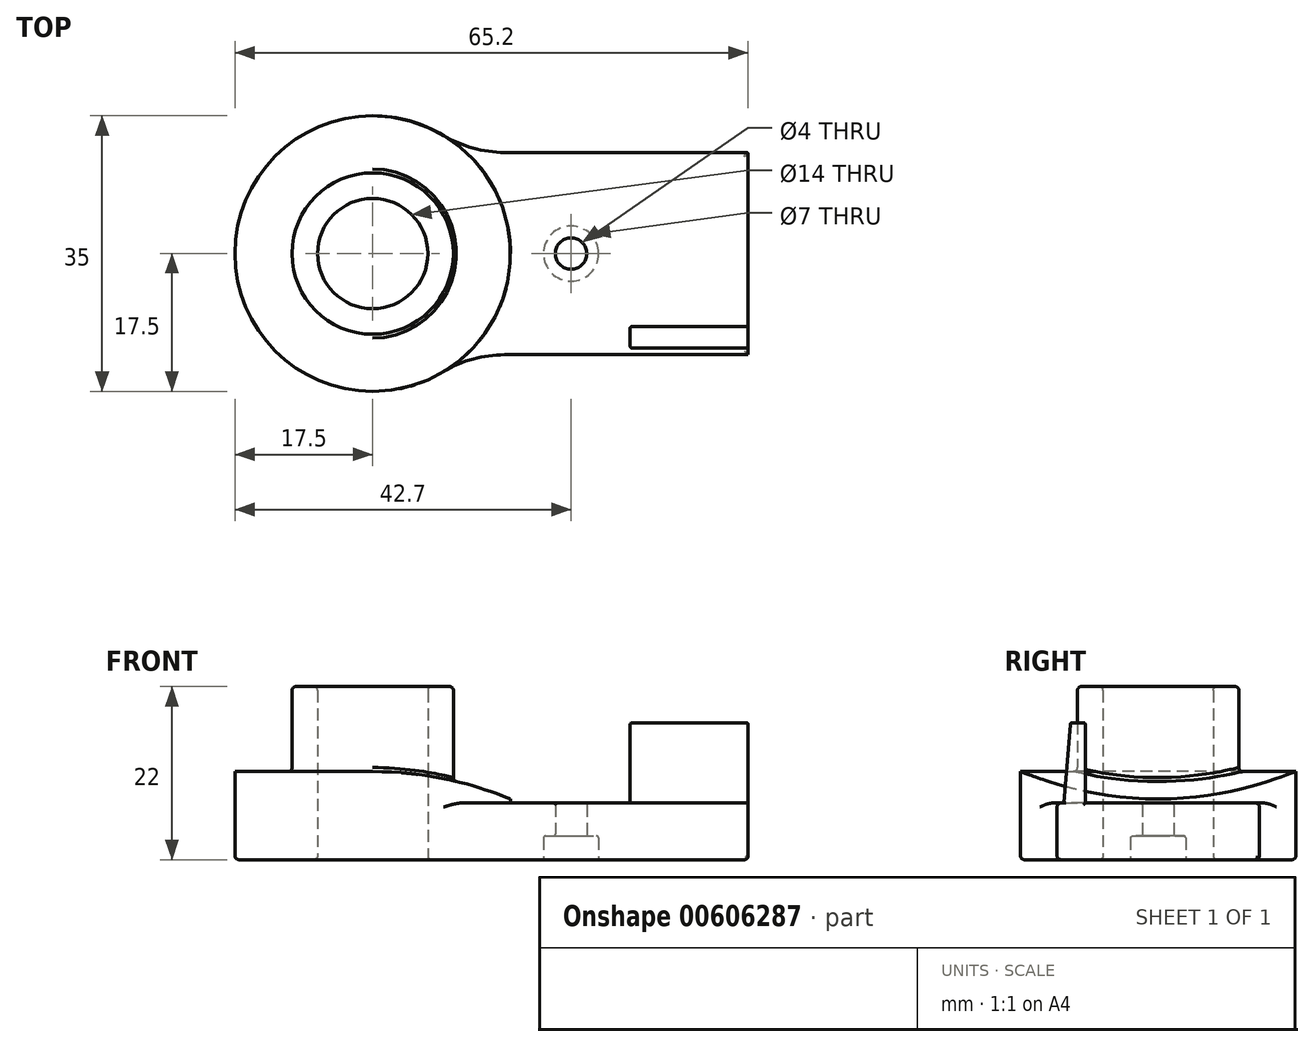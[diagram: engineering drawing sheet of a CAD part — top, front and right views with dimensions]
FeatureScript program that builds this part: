
annotation { "Feature Type Name" : "Feature", "Feature Type Description" : "" }
export const myFeature = defineFeature(function(context is Context, id is Id, definition is map)
    precondition{}
    {
        {
            var Q0;
            Q0=qCreatedBy(makeId("Top.planeOp"),FACE);
            var sketch = newSketch(context, id + "F0", { "sketchPlane" : qUnion([Q0])});
            skArc(sketch, "E0", {"start": v(11.88, 12.85) * mm, "mid": v(-17.5, 0) * mm, "end": v(11.88, -12.85) * mm});
            skLineSegment(sketch, "E1.bottom", {"start": v(11.88, 12.85) * mm, "end": v(47.7, 12.85) * mm});
            skLineSegment(sketch, "E1.top", {"start": v(11.88, -12.85) * mm, "end": v(47.7, -12.85) * mm});
            skLineSegment(sketch, "E1.right", {"start": v(47.7, 12.85) * mm, "end": v(47.7, -12.85) * mm});
            skLineSegment(sketch, "E2", {"start": v(47.7, 0) * mm, "end": v(0, 0) * mm, "construction": true});
            skCircle(sketch, "E3", {"center": v(25.2, 0) * mm, "radius": 2 * mm});
            skCircle(sketch, "E4", {"center": v(0, 0) * mm, "radius": 7 * mm});
            skPoint(sketch, "E5.orphan", {"position": v(0, 12.85) * mm});
            skPoint(sketch, "E6.trimOffspring.end.orphan", {"position": v(0, -12.85) * mm});
            skSolve(sketch);
        }
        {
            var Q0;
            Q0 = qSketchRegion(id + "F0", true);
            extrude(context, id + "F1", {"entities" : qUnion([Q0]), "depth" : 7.2 * mm, "offsetDistance" : 25 * mm});
        }
        {
            var Q0;
            Q0=makeQuery(id+"F1.opExtrude","SWEPT_FACE",FACE,{"disambiguationData":[OSD([sQuery(id+"F0.wireOp",EDGE,"E1.right")])]});
            var sketch = newSketch(context, id + "F2", { "sketchPlane" : qUnion([Q0])});
            skLineSegment(sketch, "E7", {"start": v(-9.25, 7.2) * mm, "end": v(-9.25, 17.4) * mm});
            skLineSegment(sketch, "E8", {"start": v(-9.25, 17.4) * mm, "end": v(-11.15, 17.4) * mm});
            skLineSegment(sketch, "E9", {"start": v(-11.15, 17.4) * mm, "end": v(-12, 7.2) * mm});
            skLineSegment(sketch, "E10", {"start": v(-12, 7.2) * mm, "end": v(-9.25, 7.2) * mm});
            skSolve(sketch);
        }
        {
            var Q0;
            Q0=makeQuery(id+"F2.imprint","IMPRINT",FACE,{"disambiguationData":[TD([[makeQuery(id+"F2.imprint","IMPRINT",EDGE,{"derivedFrom":sQuery(id+"F2.wireOp",EDGE,"E7")}),1.0]])]});
            extrude(context, id + "F3", {"entities" : qUnion([Q0]), "operationType" : NewBodyOperationType.ADD, "oppositeDirection" : true, "depth" : 15 * mm, "offsetDistance" : 25 * mm});
        }
        {
            var Q0;
            Q0=makeQuery(id+"F1.opExtrude","CAP_FACE",FACE,{"disambiguationData":[OSD([sQuery(id+"F0.wireOp",EDGE,"E0"),sQuery(id+"F0.wireOp",EDGE,"E1.bottom"),sQuery(id+"F0.wireOp",EDGE,"E1.top"),sQuery(id+"F0.wireOp",EDGE,"E1.right"),sQuery(id+"F0.wireOp",EDGE,"E3"),sQuery(id+"F0.wireOp",EDGE,"E4")])],"isStart":false});
            var sketch = newSketch(context, id + "F4", { "sketchPlane" : qUnion([Q0])});
            skCircle(sketch, "E11.0", {"center": v(0, 0) * mm, "radius": 7 * mm});
            skCircle(sketch, "E12", {"center": v(0, 0) * mm, "radius": 17.5 * mm});
            skSolve(sketch);
        }
        {
            var Q0;
            Q0 = qSketchRegion(id + "F4", true);
            extrude(context, id + "F5", {"entities" : qUnion([Q0]), "operationType" : NewBodyOperationType.ADD, "depth" : 4 * mm, "offsetDistance" : 25 * mm});
        }
        {
            var Q0;
            Q0=qCreatedBy(makeId("Front.planeOp"),FACE);
            var sketch = newSketch(context, id + "F6", { "sketchPlane" : qUnion([Q0])});
            skArc(sketch, "E13", {"start": v(17.5, 7.7) * mm, "mid": v(8.92, 10.32) * mm, "end": v(0, 11.2) * mm});
            skLineSegment(sketch, "E14", {"start": v(0, 11.2) * mm, "end": v(0, 14.73) * mm});
            skLineSegment(sketch, "E15", {"start": v(0, 14.73) * mm, "end": v(20.16, 14.73) * mm});
            skLineSegment(sketch, "E16", {"start": v(20.16, 14.73) * mm, "end": v(17.5, 7.7) * mm});
            skSolve(sketch);
        }
        {
            var Q0;
            Q0=makeQuery(id+"F6.imprint","IMPRINT",FACE,{"disambiguationData":[TD([[makeQuery(id+"F6.imprint","IMPRINT",EDGE,{"derivedFrom":sQuery(id+"F6.wireOp",EDGE,"E13")}),-1.0]])]});
            extrude(context, id + "F7", {"entities" : qUnion([Q0]), "operationType" : NewBodyOperationType.REMOVE, "endBound" : BoundingType.SYMMETRIC, "oppositeDirection" : true, "depth" : 35 * mm, "offsetDistance" : 25 * mm});
        }
        {
            var Q0;
            Q0=qCreatedBy(makeId("Top.planeOp"),FACE);
            var sketch = newSketch(context, id + "F8", { "sketchPlane" : qUnion([Q0])});
            skCircle(sketch, "E17", {"center": v(0, 0) * mm, "radius": 10.25 * mm});
            skCircle(sketch, "E18", {"center": v(0, 0) * mm, "radius": 7 * mm});
            skSolve(sketch);
        }
        {
            var Q0;
            Q0 = qSketchRegion(id + "F8", true);
            extrude(context, id + "F9", {"entities" : qUnion([Q0]), "operationType" : NewBodyOperationType.ADD, "depth" : 22 * mm, "offsetDistance" : 25 * mm});
        }
        {
            var Q0;
            Q0=makeQuery(id+"F1.opExtrude","SWEPT_EDGE",EDGE,{"disambiguationData":[OSD([sQuery(id+"F0.wireOp",EDGE,"E0"),sQuery(id+"F0.wireOp",EDGE,"E1.top")])]});
            var Q1;
            Q1=makeQuery(id+"F1.opExtrude","SWEPT_EDGE",EDGE,{"disambiguationData":[OSD([sQuery(id+"F0.wireOp",EDGE,"E0"),sQuery(id+"F0.wireOp",EDGE,"E1.bottom")])]});
            fillet(context, id + "F10", {"entities" : qUnion([Q0, Q1]), "radius" : 15 * mm, "tangentPropagation" : true, "allowEdgeOverflow" : false});
        }
        {
            var Q0;
            Q0=makeQuery(id+"FCpYSeTeSg7XSQh_1.1.F7.boolean.opBoolean","INTERSECT",EDGE,{"derivedFrom":[makeQuery(id+"F5.boolean.opBoolean","MERGE",FACE,{"derivedFrom":[makeQuery(id+"F1.opExtrude","SWEPT_FACE",FACE,{"disambiguationData":[OSD([sQuery(id+"F0.wireOp",EDGE,"E0")])]}),makeQuery(id+"F5.opExtrude","SWEPT_FACE",FACE,{"disambiguationData":[OSD([sQuery(id+"F4.wireOp",EDGE,"E12")])]})]}),makeQuery(id+"FCpYSeTeSg7XSQh_1.1.F7.opExtrude","SWEPT_FACE",FACE,{"disambiguationData":[OSD([sQuery(id+"F6.wireOp",EDGE,"E13")])]})]});
            var Q1;
            {var subQ0=sQuery(id+"F6.wireOp",EDGE,"E13");Q1=makeQuery(id+"F9.boolean.opBoolean","INTERSECT",EDGE,{"derivedFrom":[makeQuery(id+"FCpYSeTeSg7XSQh_1.1.F7.boolean.opBoolean","MERGE",FACE,{"derivedFrom":[makeQuery(id+"F7.boolean.opBoolean","COPY",FACE,{"derivedFrom":makeQuery(id+"F7.opExtrude","SWEPT_FACE",FACE,{"disambiguationData":[OSD([subQ0])]})}),makeQuery(id+"FCpYSeTeSg7XSQh_1.1.F7.opExtrude","SWEPT_FACE",FACE,{"disambiguationData":[OSD([subQ0])]})]}),makeQuery(id+"F9.opExtrude","SWEPT_FACE",FACE,{"disambiguationData":[OSD([sQuery(id+"F8.wireOp",EDGE,"E17")])]})]});}
            var Q2;
            Q2=makeQuery(id+"F9.opExtrude","CAP_EDGE",EDGE,{"disambiguationData":[OSD([sQuery(id+"F8.wireOp",EDGE,"E17")])],"isStart":false});
            var Q3;
            Q3=makeQuery(id+"F9.opExtrude","CAP_EDGE",EDGE,{"disambiguationData":[OSD([sQuery(id+"F8.wireOp",EDGE,"E18")])],"isStart":false});
            var Q4;
            Q4=makeQuery(id+"F1.opExtrude","CAP_EDGE",EDGE,{"disambiguationData":[OSD([sQuery(id+"F0.wireOp",EDGE,"E1.top")])],"isStart":false});
            var Q5;
            Q5=makeQuery(id+"F1.opExtrude","CAP_EDGE",EDGE,{"disambiguationData":[OSD([sQuery(id+"F0.wireOp",EDGE,"E1.bottom")])],"isStart":false});
            var Q6;
            Q6=makeQuery(id+"F1.opExtrude","CAP_EDGE",EDGE,{"disambiguationData":[OSD([sQuery(id+"F0.wireOp",EDGE,"E1.top")])],"isStart":true});
            var Q7;
            Q7=makeQuery(id+"F1.opExtrude","CAP_EDGE",EDGE,{"disambiguationData":[OSD([sQuery(id+"F0.wireOp",EDGE,"E1.right")])],"isStart":true});
            var Q8;
            Q8=makeQuery(id+"F1.opExtrude","CAP_EDGE",EDGE,{"disambiguationData":[OSD([sQuery(id+"F0.wireOp",EDGE,"E4")])],"isStart":true});
            fillet(context, id + "F11", {"entities" : qUnion([Q0, Q1, Q2, Q3, Q4, Q5, Q6, Q7, Q8]), "radius" : 0.5 * mm, "tangentPropagation" : true, "allowEdgeOverflow" : false});
        }
        {
            var Q0;
            Q0=makeQuery(id+"F1.opExtrude","CAP_FACE",FACE,{"disambiguationData":[OSD([sQuery(id+"F0.wireOp",EDGE,"E0"),sQuery(id+"F0.wireOp",EDGE,"E1.bottom"),sQuery(id+"F0.wireOp",EDGE,"E1.top"),sQuery(id+"F0.wireOp",EDGE,"E1.right"),sQuery(id+"F0.wireOp",EDGE,"E3"),sQuery(id+"F0.wireOp",EDGE,"E4")])],"isStart":true});
            var sketch = newSketch(context, id + "F12", { "sketchPlane" : qUnion([Q0])});
            skCircle(sketch, "E19", {"center": v(25.2, 0) * mm, "radius": 3.5 * mm});
            skSolve(sketch);
        }
        {
            var Q0;
            Q0 = qSketchRegion(id + "F12", true);
            extrude(context, id + "F13", {"entities" : qUnion([Q0]), "operationType" : NewBodyOperationType.REMOVE, "oppositeDirection" : true, "depth" : 3 * mm, "offsetDistance" : 25 * mm});
        }
        {
            var Q0;
            Q0=makeQuery(id+"F3.opExtrude","SWEPT_FACE",FACE,{"disambiguationData":[OSD([sQuery(id+"F2.wireOp",EDGE,"E8")])]});
            var Q1;
            Q1=makeQuery(id+"FFUPkmP4B0qJaFo_1.1.F3.opExtrude","SWEPT_FACE",FACE,{"disambiguationData":[OSD([sQuery(id+"F2.wireOp",EDGE,"E8")])]});
            var Q2;
            Q2=makeQuery(id+"F3.opExtrude","CAP_EDGE",EDGE,{"disambiguationData":[OSD([sQuery(id+"F2.wireOp",EDGE,"E7")])],"isStart":true});
            var Q3;
            Q3=makeQuery(id+"F3.opExtrude","CAP_EDGE",EDGE,{"disambiguationData":[OSD([sQuery(id+"F2.wireOp",EDGE,"E9")])],"isStart":true});
            var Q4;
            {var subQ3=sQuery(id+"F2.wireOp",EDGE,"E7");var subQ5=sQuery(id+"F0.wireOp",EDGE,"E1.right");var subQ6=sQuery(id+"F0.wireOp",EDGE,"E1.bottom");var subQ8=makeQuery(id+"F3.opExtrude","SWEPT_FACE",FACE,{"disambiguationData":[OSD([subQ3])]});Q4=makeQuery(id+"FFUPkmP4B0qJaFo_1.1.F3.boolean.opBoolean","SPLIT",EDGE,{"disambiguationData":[TD([subQ8])],"derivedFrom":makeQuery(id+"F3.boolean.opBoolean","SPLIT",EDGE,{"disambiguationData":[TD([makeQuery(id+"F1.opExtrude","SWEPT_FACE",FACE,{"disambiguationData":[OSD([subQ6])]})])],"derivedFrom":makeQuery(id+"F1.opExtrude","CAP_EDGE",EDGE,{"disambiguationData":[OSD([subQ5])],"isStart":false})})});}
            var Q5;
            Q5=makeQuery(id+"FFUPkmP4B0qJaFo_1.1.F3.opExtrude","CAP_EDGE",EDGE,{"disambiguationData":[OSD([sQuery(id+"F2.wireOp",EDGE,"E7")])],"isStart":true});
            var Q6;
            Q6=makeQuery(id+"FFUPkmP4B0qJaFo_1.1.F3.opExtrude","SWEPT_EDGE",EDGE,{"disambiguationData":[OSD([sQuery(id+"F0.wireOp",EDGE,"E1.right"),sQuery(id+"F2.wireOp",EDGE,"E7"),sQuery(id+"F2.wireOp",EDGE,"E10")])]});
            var Q7;
            Q7=makeQuery(id+"FFUPkmP4B0qJaFo_1.1.F3.opExtrude","CAP_EDGE",EDGE,{"disambiguationData":[OSD([sQuery(id+"F2.wireOp",EDGE,"E7")])],"isStart":false});
            var Q8;
            Q8=makeQuery(id+"FFUPkmP4B0qJaFo_1.1.F3.opExtrude","CAP_EDGE",EDGE,{"disambiguationData":[OSD([sQuery(id+"F2.wireOp",EDGE,"E9")])],"isStart":true});
            var Q9;
            Q9=makeQuery(id+"F3.opExtrude","CAP_EDGE",EDGE,{"disambiguationData":[OSD([sQuery(id+"F2.wireOp",EDGE,"E9")])],"isStart":false});
            var Q10;
            Q10=makeQuery(id+"F3.opExtrude","SWEPT_EDGE",EDGE,{"disambiguationData":[OSD([sQuery(id+"F0.wireOp",EDGE,"E1.right"),sQuery(id+"F2.wireOp",EDGE,"E9"),sQuery(id+"F2.wireOp",EDGE,"E10")])]});
            var Q11;
            Q11=makeQuery(id+"F3.opExtrude","CAP_EDGE",EDGE,{"disambiguationData":[OSD([sQuery(id+"F2.wireOp",EDGE,"E7")])],"isStart":false});
            var Q12;
            Q12=makeQuery(id+"F3.opExtrude","SWEPT_EDGE",EDGE,{"disambiguationData":[OSD([sQuery(id+"F0.wireOp",EDGE,"E1.right"),sQuery(id+"F2.wireOp",EDGE,"E7"),sQuery(id+"F2.wireOp",EDGE,"E10")])]});
            var Q13;
            Q13=makeQuery(id+"FFUPkmP4B0qJaFo_1.1.F3.opExtrude","CAP_EDGE",EDGE,{"disambiguationData":[OSD([sQuery(id+"F2.wireOp",EDGE,"E9")])],"isStart":false});
            var Q14;
            Q14=makeQuery(id+"FFUPkmP4B0qJaFo_1.1.F3.opExtrude","SWEPT_EDGE",EDGE,{"disambiguationData":[OSD([sQuery(id+"F0.wireOp",EDGE,"E1.right"),sQuery(id+"F2.wireOp",EDGE,"E9"),sQuery(id+"F2.wireOp",EDGE,"E10")])]});
            var Q15;
            Q15=makeQuery(id+"F5.opExtrude","CAP_EDGE",EDGE,{"disambiguationData":[OSD([sQuery(id+"F4.wireOp",EDGE,"E12")])],"isStart":true});
            var Q16;
            Q16=makeQuery(id+"F13.boolean.opBoolean","COPY",EDGE,{"derivedFrom":makeQuery(id+"F13.opExtrude","CAP_EDGE",EDGE,{"disambiguationData":[OSD([sQuery(id+"F12.wireOp",EDGE,"E19")])],"isStart":false})});
            var Q17;
            Q17=makeQuery(id+"F13.boolean.opBoolean","INTERSECT",EDGE,{"derivedFrom":[makeQuery(id+"F1.opExtrude","SWEPT_FACE",FACE,{"disambiguationData":[OSD([sQuery(id+"F0.wireOp",EDGE,"E3")])]}),makeQuery(id+"F13.opExtrude","CAP_FACE",FACE,{"disambiguationData":[OSD([sQuery(id+"F12.wireOp",EDGE,"E19")])],"isStart":false})]});
            var Q18;
            Q18=makeQuery(id+"F13.boolean.opBoolean","COPY",EDGE,{"derivedFrom":makeQuery(id+"F13.opExtrude","CAP_EDGE",EDGE,{"disambiguationData":[OSD([sQuery(id+"F12.wireOp",EDGE,"E19")])],"isStart":true})});
            var Q19;
            Q19=makeQuery(id+"F1.opExtrude","CAP_EDGE",EDGE,{"disambiguationData":[OSD([sQuery(id+"F0.wireOp",EDGE,"E3")])],"isStart":false});
            fillet(context, id + "F14", {"entities" : qUnion([Q0, Q1, Q2, Q3, Q4, Q5, Q6, Q7, Q8, Q9, Q10, Q11, Q12, Q13, Q14, Q15, Q16, Q17, Q18, Q19]), "radius" : 0.25 * mm, "tangentPropagation" : true, "allowEdgeOverflow" : false});
        }
    });
